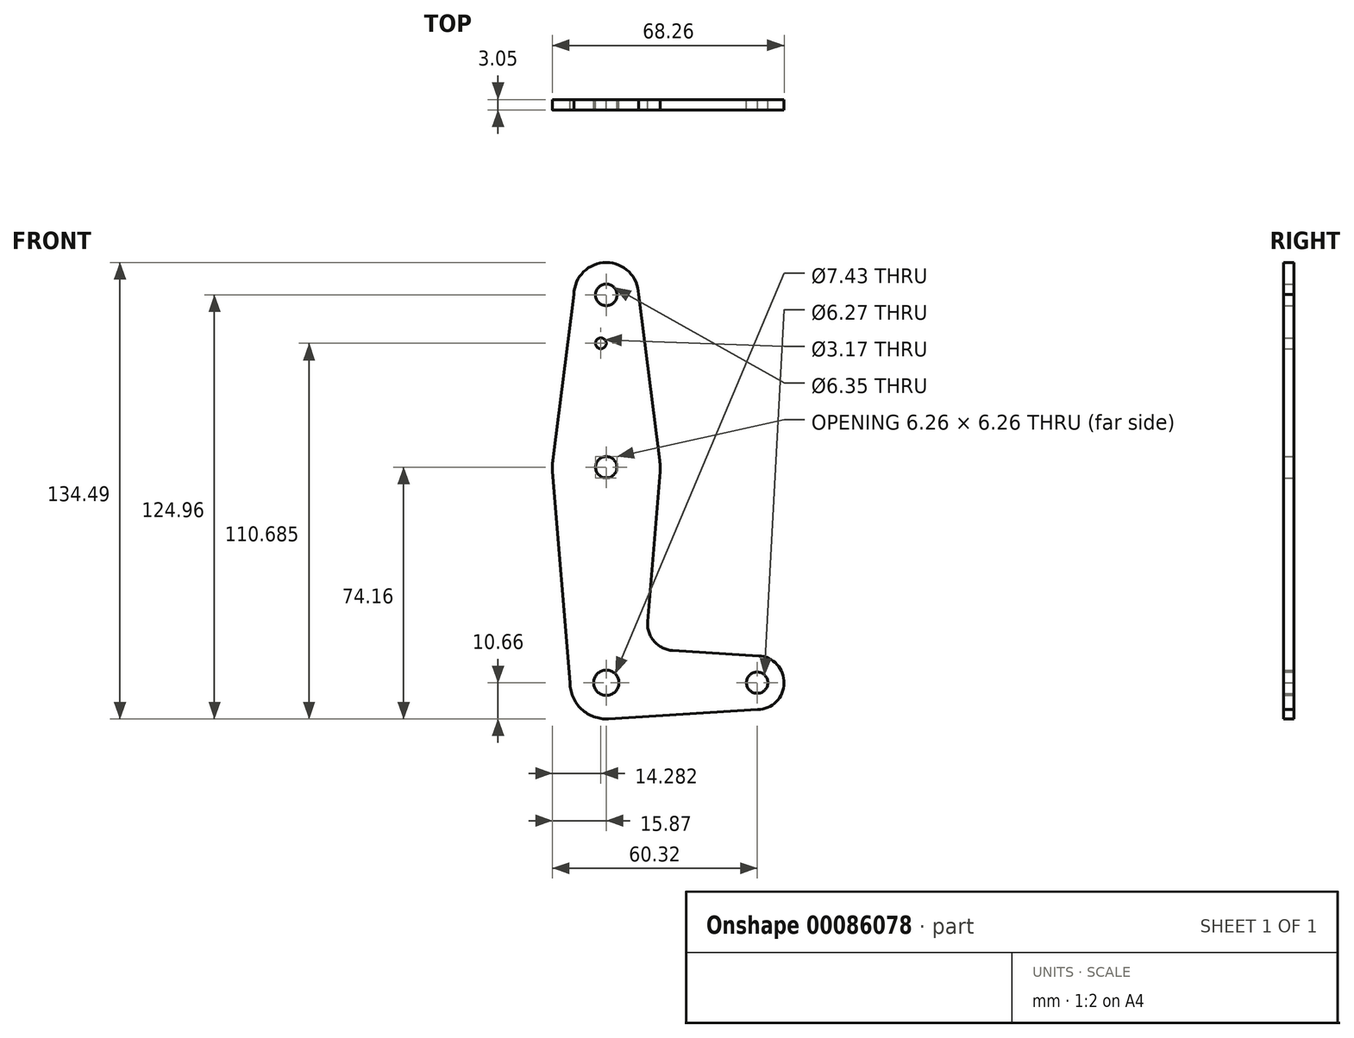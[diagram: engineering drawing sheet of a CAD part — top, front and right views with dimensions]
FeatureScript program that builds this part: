
annotation { "Feature Type Name" : "Feature", "Feature Type Description" : "" }
export const myFeature = defineFeature(function(context is Context, id is Id, definition is map)
    precondition{}
    {
        {
            var Q0;
            Q0=qCreatedBy(makeId("Front.planeOp"),FACE);
            var sketch = newSketch(context, id + "F0", { "sketchPlane" : qUnion([Q0])});
            skLineSegment(sketch, "E0", {"start": v(0, 0) * mm, "end": v(44.45, 0) * mm});
            skCircle(sketch, "E1", {"center": v(0, 114.3) * mm, "radius": 9.52 * mm});
            skCircle(sketch, "E2", {"center": v(0, 63.5) * mm, "radius": 15.88 * mm});
            skCircle(sketch, "E3", {"center": v(0, 0) * mm, "radius": 10.66 * mm});
            skCircle(sketch, "E4", {"center": v(44.45, 0) * mm, "radius": 7.94 * mm});
            skLineSegment(sketch, "E5", {"start": v(0, 63.5) * mm, "end": v(0, 114.3) * mm});
            skLineSegment(sketch, "E6", {"start": v(0, 0) * mm, "end": v(0, 63.5) * mm});
            skLineSegment(sketch, "E7", {"start": v(9.52, 114.46) * mm, "end": v(15.75, 65.5) * mm});
            skLineSegment(sketch, "E8", {"start": v(-9.52, 114.46) * mm, "end": v(-15.75, 65.5) * mm});
            skLineSegment(sketch, "E9", {"start": v(-10.66, 0) * mm, "end": v(-15.82, 62.19) * mm});
            skLineSegment(sketch, "E10", {"start": v(12.16, 18.07) * mm, "end": v(15.82, 62.19) * mm});
            skLineSegment(sketch, "E11", {"start": v(44.6, -7.94) * mm, "end": v(0.66, -10.64) * mm});
            skLineSegment(sketch, "E12", {"start": v(44.92, 7.92) * mm, "end": v(19.6, 9.48) * mm});
            skCircle(sketch, "E13", {"center": v(0, 114.3) * mm, "radius": 3.18 * mm});
            skCircle(sketch, "E14", {"center": v(-1.59, 100.03) * mm, "radius": 1.59 * mm});
            skCircle(sketch, "E15", {"center": v(0, 63.5) * mm, "radius": 3.13 * mm});
            skCircle(sketch, "E16", {"center": v(0, 0) * mm, "radius": 3.72 * mm});
            skCircle(sketch, "E17", {"center": v(44.45, 0) * mm, "radius": 3.14 * mm});
            skArc(sketch, "E18.filletArc", {"start": v(12.16, 18.07) * mm, "mid": v(14.07, 12.21) * mm, "end": v(19.6, 9.48) * mm});
            skSolve(sketch);
        }
        {
            var Q0;
            Q0 = qSketchRegion(id + "F0", true);
            var Q1;
            {var subQ0=sQuery(id+"F0.wireOp",EDGE,"E16");var subQ1=sQuery(id+"F0.wireOp",EDGE,"E0");var subQ2=makeQuery(id+"F0.imprint","INTERSECT",VERTEX,{"derivedFrom":[subQ1,subQ0]});Q1=makeQuery(id+"F0.imprint","IMPRINT",FACE,{"disambiguationData":[TD([[makeQuery(id+"F0.imprint","IMPRINT",EDGE,{"disambiguationData":[TD([[subQ2,-1.0]])],"derivedFrom":subQ1}),1.0]])]});}
            extrude(context, id + "F1", {"entities" : qUnion([Q0, Q1]), "depth" : 3.05 * mm});
        }
    });
